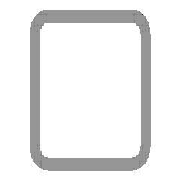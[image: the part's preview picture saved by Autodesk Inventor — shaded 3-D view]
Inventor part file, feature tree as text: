
AUTODESK INVENTOR PART (.ipt)
format: ipt  version: 2025.1 (Build 291241020, 241B)  size: 134,144 bytes
history: native  units: mm (DEFAULTED — no unit token found)
features: other x4, sketch x1, plane x1
ambient origin geometry x8: Origin, YZ Plane, XZ Plane, XY Plane, X Axis, Y Axis, Z Axis, Center Point
bodies: Solid1 (feature_tree), Body (feature_tree)
feature tree (6):
  parser-record x1  (decoder bookkeeping rows leaked as tree rows — omitted from the tree; the rows remain in map.json)
  other  "Driven Length"
  other  "Start Plane"
  other  "End Plane"
  sketch  "Sketch3"  dims[d3=790.0mm d4=0.0mm d7=8.0mm d9=100.0mm d11=100.0mm d12=4.0mm d13=100.0mm d14=890.0mm d15=50.0mm d16=50.0mm d17=90.0deg d18=790.0mm]
  plane  "Work Plane3"
